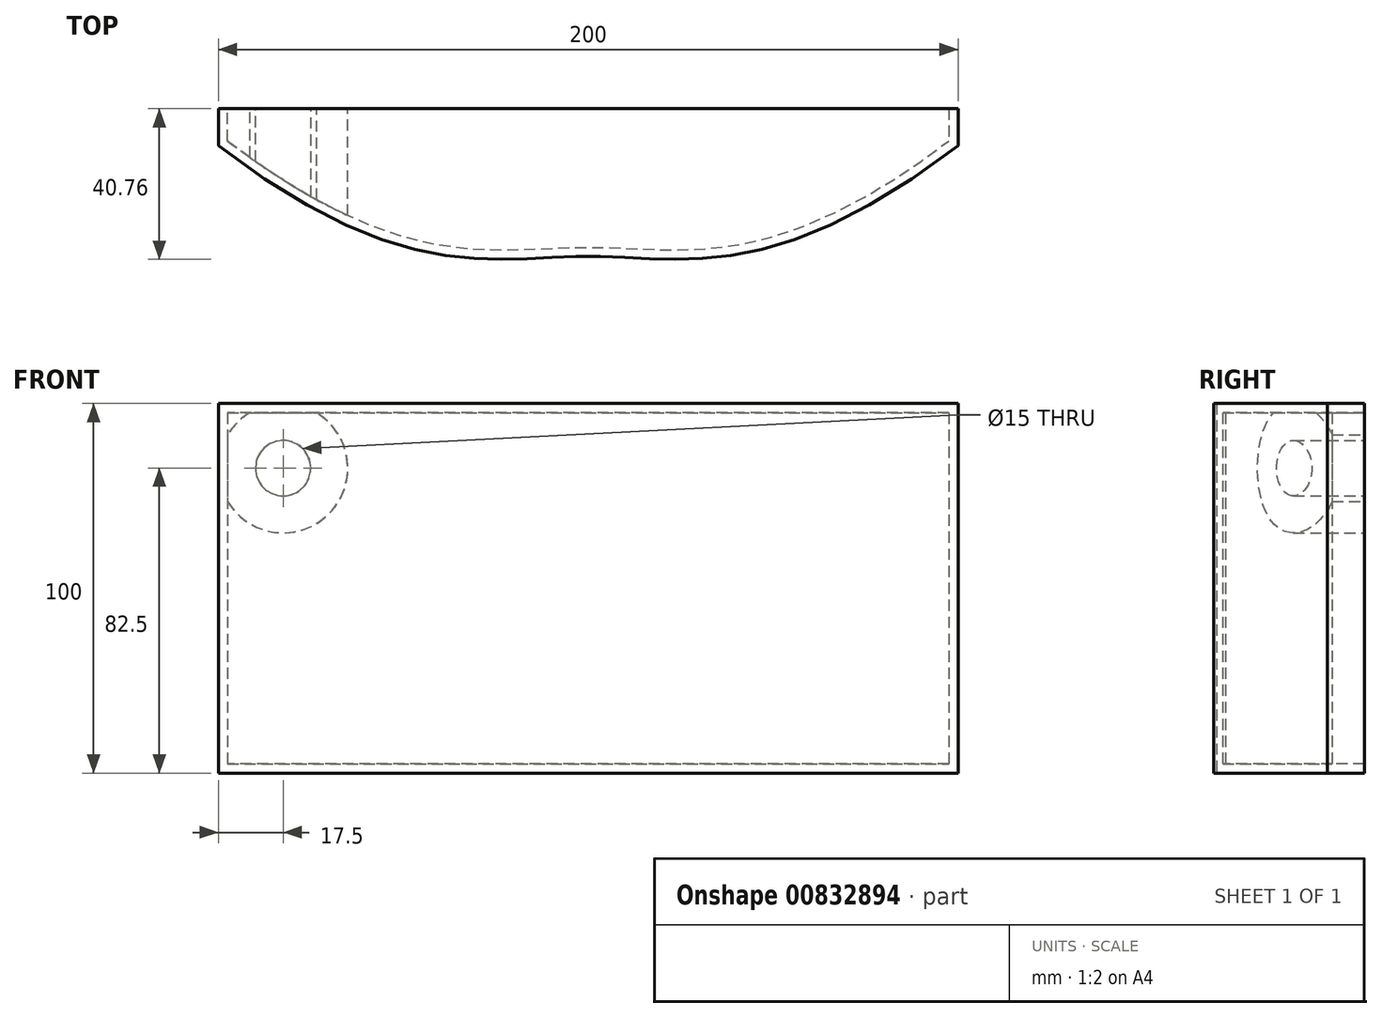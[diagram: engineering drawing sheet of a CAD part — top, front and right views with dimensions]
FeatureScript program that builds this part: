
annotation { "Feature Type Name" : "Feature", "Feature Type Description" : "" }
export const myFeature = defineFeature(function(context is Context, id is Id, definition is map)
    precondition{}
    {
        {
            var Q0;
            Q0=qCreatedBy(makeId("Top.planeOp"),FACE);
            var sketch = newSketch(context, id + "F0", { "sketchPlane" : qUnion([Q0])});
            skLineSegment(sketch, "E0", {"start": v(100, 9.99) * mm, "end": v(-100, 9.99) * mm});
            skLineSegment(sketch, "E1", {"start": v(-100, 9.99) * mm, "end": v(-100, 0) * mm});
            skLineSegment(sketch, "E2", {"start": v(100, 9.99) * mm, "end": v(100, 0) * mm});
            skFitSpline(sketch, "E3", {"points": [v(-100, 0) * mm, v(0, -30) * mm, v(100, 0) * mm], "startDerivative": vector(300, -230) * mm, "endDerivative": vector(300, 230) * mm});
            skSolve(sketch);
        }
        {
            var Q0;
            Q0=makeQuery(id+"F0.imprint","IMPRINT",FACE,{"disambiguationData":[TD([[makeQuery(id+"F0.imprint","IMPRINT",EDGE,{"derivedFrom":sQuery(id+"F0.wireOp",EDGE,"E0")}),1.0]])]});
            extrude(context, id + "F1", {"entities" : qUnion([Q0]), "depth" : 100 * mm, "offsetDistance" : 25 * mm, "symmetric" : true});
        }
        {
            var Q0;
            Q0=makeQuery(id+"F1.opExtrude","SWEPT_FACE",FACE,{"disambiguationData":[OSD([sQuery(id+"F0.wireOp",EDGE,"E0")])]});
            shell(context, id + "F2", {"entities" : qUnion([Q0]), "thickness" : 2.5 * mm});
        }
        {
            var Q0;
            Q0=makeQuery(id+"F1.opExtrude","SWEPT_FACE",FACE,{"disambiguationData":[OSD([sQuery(id+"F0.wireOp",EDGE,"E0")])]});
            var sketch = newSketch(context, id + "F3", { "sketchPlane" : qUnion([Q0])});
            skLineSegment(sketch, "E4", {"start": v(97.5, 47.5) * mm, "end": v(82.5, 47.5) * mm});
            skLineSegment(sketch, "E5", {"start": v(82.5, 47.5) * mm, "end": v(82.5, 32.5) * mm});
            skCircle(sketch, "E6", {"center": v(82.5, 32.5) * mm, "radius": 7.5 * mm});
            skCircle(sketch, "E7", {"center": v(82.5, 32.5) * mm, "radius": 17.5 * mm});
            skSolve(sketch);
        }
        {
            var Q0;
            Q0=makeQuery(id+"F3.imprint","IMPRINT",FACE,{"disambiguationData":[TD([[makeQuery(id+"F3.imprint","IMPRINT",EDGE,{"derivedFrom":sQuery(id+"F3.wireOp",EDGE,"E6")}),-1.0]])]});
            extrude(context, id + "F4", {"entities" : qUnion([Q0]), "endBound" : BoundingType.UP_TO_NEXT, "oppositeDirection" : true, "depth" : 25 * mm, "offsetDistance" : 25 * mm});
        }
    });
